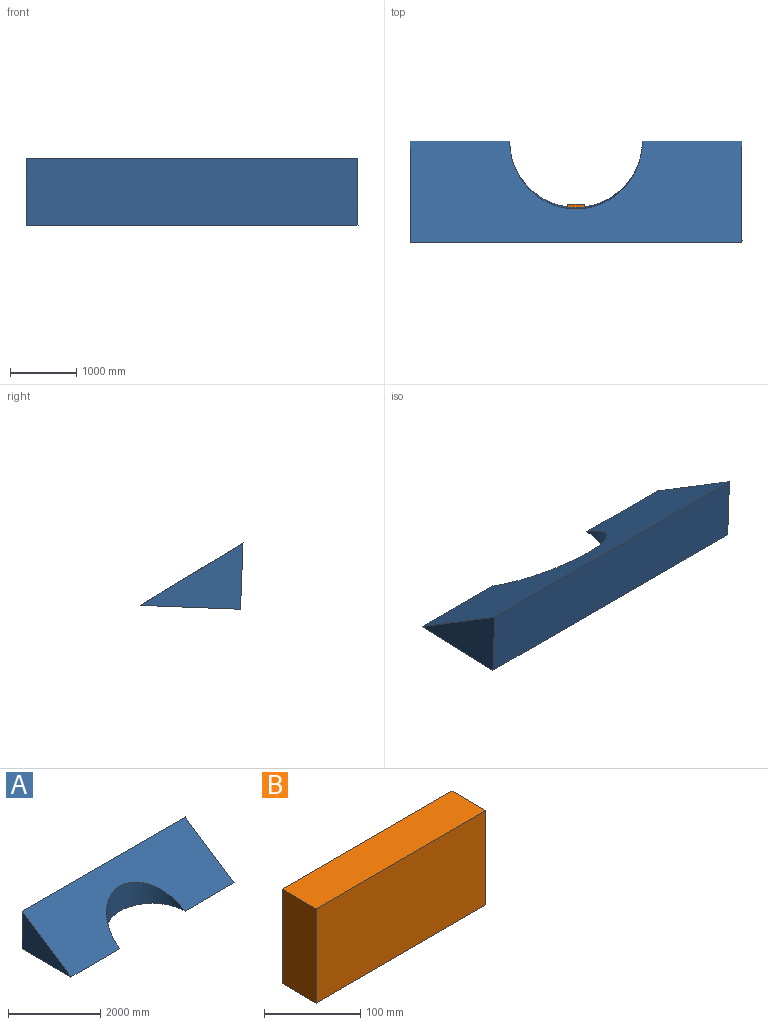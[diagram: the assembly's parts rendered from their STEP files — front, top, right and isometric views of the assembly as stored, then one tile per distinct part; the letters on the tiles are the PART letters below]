
ASSEMBLY  parts=2 mates=1
PART A: 6 faces, bbox 5000x1500x1000 mm
  f0: plane 5000x1500mm, normal (0,-0.55,0.83), area 7126016mm2, adj f1,f2,f3,f4,f5
  f1: plane 5000x1500mm, normal (0,0,-1), area 5929203.7mm2, adj f0,f2,f3,f4,f5
  f2: plane 5000x1000mm, normal (0,1,0), area 5000000mm2, adj f0,f1,f3,f4
  f3: plane 1500x1000mm, normal (1,0,0), area 750000mm2, adj f0,f1,f2
  f4: plane 1500x1000mm, normal (-1,0,0), area 750000mm2, adj f0,f1,f2
  f5: cylinder r=1000mm len=2000mm, axis (0,0,-1), area 1333332.3mm2, adj f0,f1
PART B: 6 faces, bbox 250x50x120 mm
  f0: plane 250x50mm, normal (0,0,1), area 12500mm2, adj f1,f3,f4,f5
  f1: plane 120x50mm, normal (-1,0,0), area 6000mm2, adj f0,f2,f4,f5
  f2: plane 250x50mm, normal (0,0,-1), area 12500mm2, adj f1,f3,f4,f5
  f3: plane 120x50mm, normal (1,0,0), area 6000mm2, adj f0,f2,f4,f5
  f4: plane 250x120mm, normal (0,-1,0), area 30000mm2, adj f0,f1,f2,f3
  f5: plane 250x120mm, normal (0,1,0), area 30000mm2, adj f0,f1,f2,f3
PLACE A rot(axis=(0,0.02,-1),180deg) t=(20.14,1864.29,71.19)mm fixed
PLACE B rot(axis=(-1,0,0),177.8deg) t=(20.12,887.7,93.73)mm
MATE planar B.f0 <-> A.f1  axis (0,0.04,-1) through (20.15,890.01,33.77)mm
